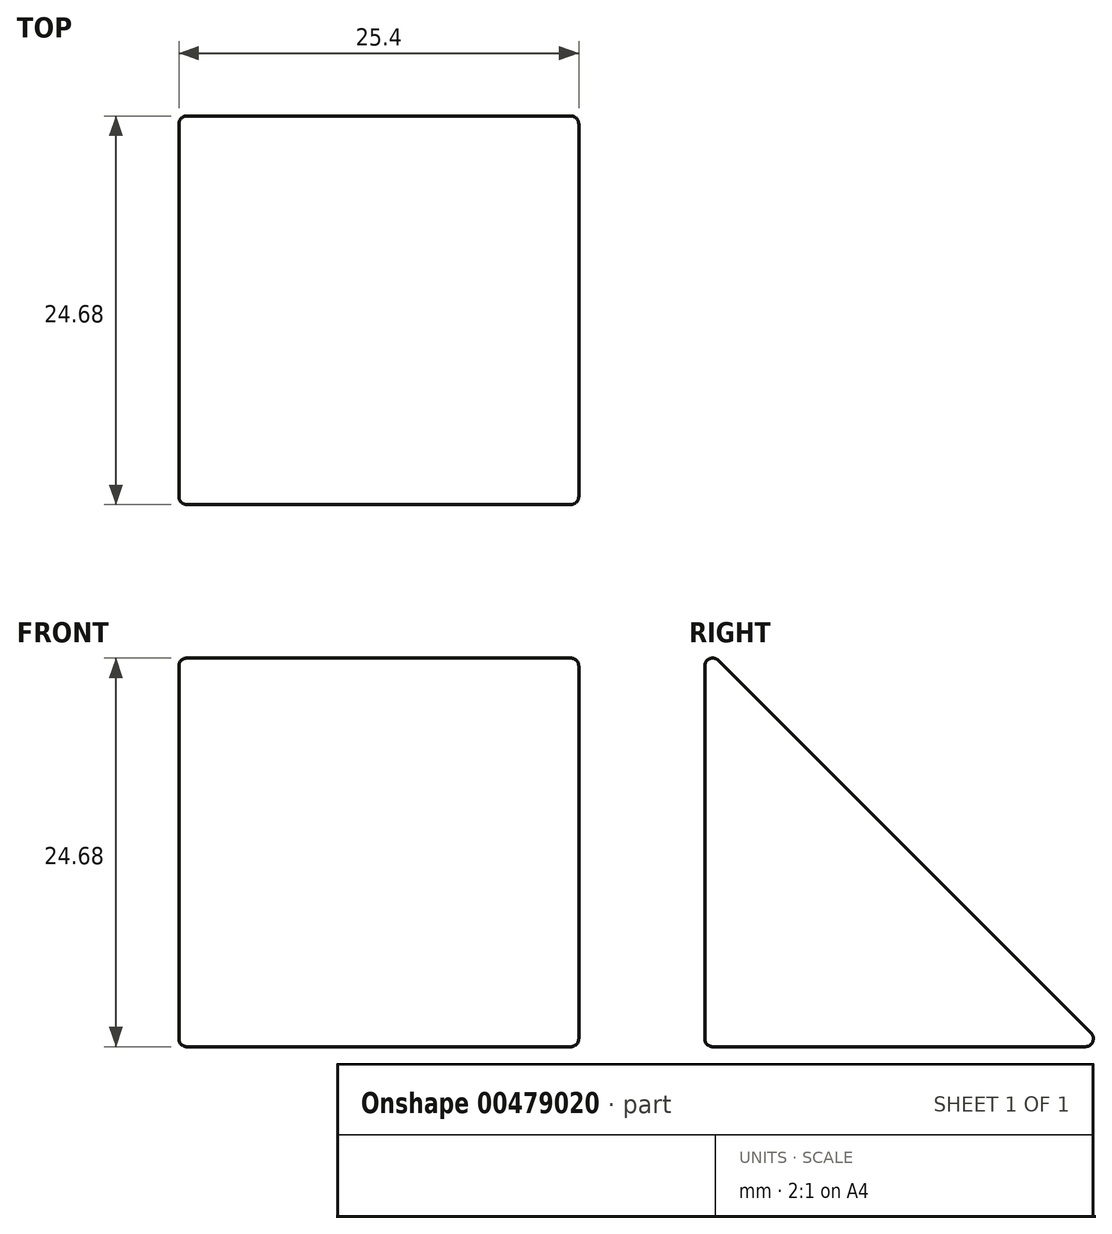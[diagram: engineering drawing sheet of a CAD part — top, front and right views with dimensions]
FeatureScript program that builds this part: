
annotation { "Feature Type Name" : "Feature", "Feature Type Description" : "" }
export const myFeature = defineFeature(function(context is Context, id is Id, definition is map)
    precondition{}
    {
        {
            var Q0;
            Q0=qCreatedBy(makeId("Front.planeOp"),FACE);
            var sketch = newSketch(context, id + "F0", { "sketchPlane" : qUnion([Q0])});
            skLineSegment(sketch, "E0.bottom", {"start": v(0, 0) * mm, "end": v(25.4, 0) * mm});
            skLineSegment(sketch, "E0.top", {"start": v(0, 25.4) * mm, "end": v(25.4, 25.4) * mm});
            skLineSegment(sketch, "E0.left", {"start": v(0, 0) * mm, "end": v(0, 25.4) * mm});
            skLineSegment(sketch, "E0.right", {"start": v(25.4, 0) * mm, "end": v(25.4, 25.4) * mm});
            skSolve(sketch);
        }
        {
            var Q0;
            Q0=makeQuery(id+"F0.imprint","IMPRINT",FACE,{"disambiguationData":[TD([[makeQuery(id+"F0.imprint","IMPRINT",EDGE,{"derivedFrom":sQuery(id+"F0.wireOp",EDGE,"E0.bottom")}),1.0]])]});
            extrude(context, id + "F1", {"entities" : qUnion([Q0]), "depth" : 25.4 * mm});
        }
        {
            var Q0;
            Q0=makeQuery(id+"F1.opExtrude","SWEPT_FACE",FACE,{"disambiguationData":[OSD([sQuery(id+"F0.wireOp",EDGE,"E0.right")])]});
            var sketch = newSketch(context, id + "F2", { "sketchPlane" : qUnion([Q0])});
            skLineSegment(sketch, "E1", {"start": v(-25.4, 25.4) * mm, "end": v(0, 0) * mm});
            skLineSegment(sketch, "E2", {"start": v(0, 0) * mm, "end": v(0, 25.4) * mm});
            skLineSegment(sketch, "E3", {"start": v(0, 25.4) * mm, "end": v(-25.4, 25.4) * mm});
            skSolve(sketch);
        }
        {
            var Q0;
            Q0=makeQuery(id+"F2.imprint","IMPRINT",FACE,{"disambiguationData":[TD([[makeQuery(id+"F2.imprint","IMPRINT",EDGE,{"derivedFrom":sQuery(id+"F2.wireOp",EDGE,"E1")}),1.0]])]});
            extrude(context, id + "F3", {"entities" : qUnion([Q0]), "operationType" : NewBodyOperationType.REMOVE, "oppositeDirection" : true, "depth" : 25.4 * mm});
        }
        {
            var Q0;
            Q0=makeQuery(id+"F1.opExtrude","CAP_FACE",FACE,{"disambiguationData":[OSD([sQuery(id+"F0.wireOp",EDGE,"E0.bottom"),sQuery(id+"F0.wireOp",EDGE,"E0.top"),sQuery(id+"F0.wireOp",EDGE,"E0.left"),sQuery(id+"F0.wireOp",EDGE,"E0.right")])],"isStart":false});
            var Q1;
            Q1=makeQuery(id+"F1.opExtrude","SWEPT_FACE",FACE,{"disambiguationData":[OSD([sQuery(id+"F0.wireOp",EDGE,"E0.right")])]});
            var Q2;
            Q2=makeQuery(id+"F3.boolean.opBoolean","COPY",FACE,{"derivedFrom":makeQuery(id+"F3.opExtrude","SWEPT_FACE",FACE,{"disambiguationData":[OSD([sQuery(id+"F2.wireOp",EDGE,"E1")])]})});
            var Q3;
            Q3=makeQuery(id+"F1.opExtrude","SWEPT_FACE",FACE,{"disambiguationData":[OSD([sQuery(id+"F0.wireOp",EDGE,"E0.bottom")])]});
            fillet(context, id + "F4", {"entities" : qUnion([Q0, Q1, Q2, Q3]), "radius" : 0.5 * mm, "tangentPropagation" : true, "allowEdgeOverflow" : false});
        }
    });
